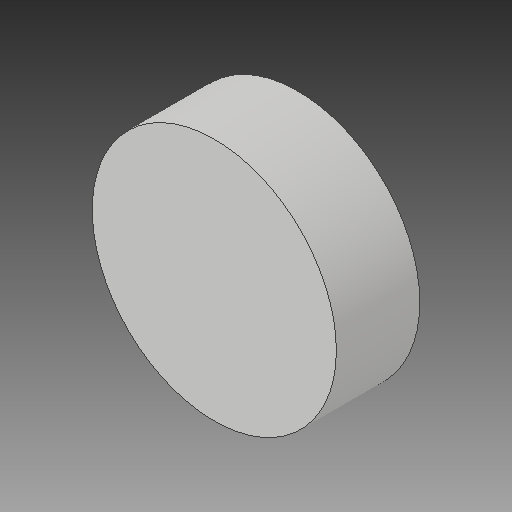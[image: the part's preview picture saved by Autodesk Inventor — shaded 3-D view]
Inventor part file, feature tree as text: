
AUTODESK INVENTOR PART (.ipt)
format: ipt  version: 2018 (Build 220112000, 112)  size: 102,400 bytes
history: native  units: mm
features: other x3, extrude x2, sketch x2, reference x1, projected_geometry x1
ambient origin geometry x8: Origin, YZ Plane, XZ Plane, XY Plane, X Axis, Y Axis, Z Axis, Center Point
bodies: Solid1 (feature_tree)
feature tree (9):
  extrude  "Extrusion1"  Depth=12.0mm
  extrude  "Extrusion2"  Depth=1.0mm TaperAngle=0.0deg
  sketch  "Sketch1"  dims[d0=5.75mm d1=12.0mm]
  reference  "Reference1"
  sketch  "Sketch2"  dims[d2=3.1mm d3=0.0mm d4=1.0mm d5=0.0mm]
  projected_geometry  "Projected Loop1"
  other  "<userpath>\OneDrive\Documents\Inventor\TSA\2018\Animatronics\Tortoise\Turtle3.iam"
  other  "Turtle3.iam"
  other  "Frame - Copy:1"
